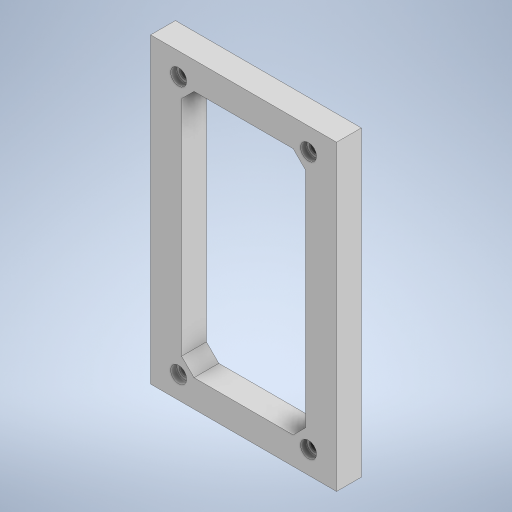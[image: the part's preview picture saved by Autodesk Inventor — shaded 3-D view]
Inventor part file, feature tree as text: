
AUTODESK INVENTOR PART (.ipt)
format: ipt  version: 2023 (Build 270158000, 158)  size: 269,312 bytes
history: native  units: mm
features: extrude x2, sketch x2, other x1
ambient origin geometry x8: Origin, YZ Plane, XZ Plane, XY Plane, X Axis, Y Axis, Z Axis, Center Point
bodies: Body1 (feature_tree)
feature tree (5):
  other  "솔리드1"
  extrude  "돌출1"  Depth=52.4mm
  extrude  "돌출2"  Depth=104.0mm
  sketch  "스케치1"
  sketch  "스케치2"
